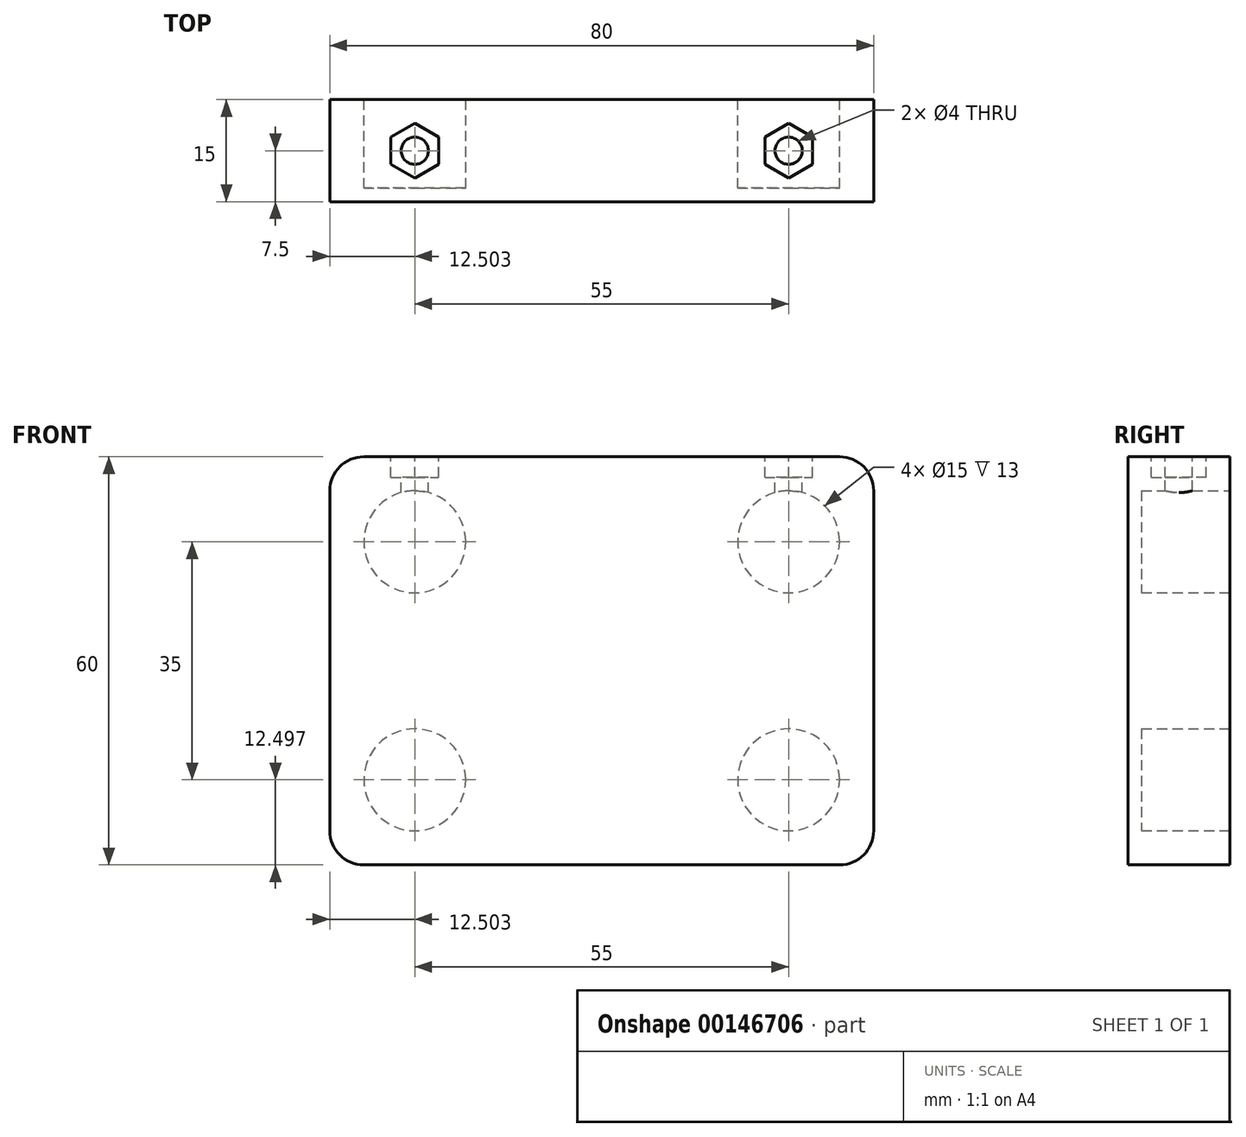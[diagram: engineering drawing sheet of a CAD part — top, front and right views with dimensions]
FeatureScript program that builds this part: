
annotation { "Feature Type Name" : "Feature", "Feature Type Description" : "" }
export const myFeature = defineFeature(function(context is Context, id is Id, definition is map)
    precondition{}
    {
        {
            var Q0;
            Q0=qCreatedBy(makeId("Front.planeOp"),FACE);
            var sketch = newSketch(context, id + "F0", { "sketchPlane" : qUnion([Q0])});
            skLineSegment(sketch, "E0.bottom", {"start": v(-70.09, 32.8) * mm, "end": v(-0.09, 32.8) * mm});
            skLineSegment(sketch, "E0.top", {"start": v(-70.09, -27.2) * mm, "end": v(-0.09, -27.2) * mm});
            skLineSegment(sketch, "E0.left", {"start": v(-75.09, 27.8) * mm, "end": v(-75.09, -22.2) * mm});
            skLineSegment(sketch, "E0.right", {"start": v(4.91, 27.8) * mm, "end": v(4.91, -22.2) * mm});
            skArc(sketch, "E1", {"start": v(-70.09, 32.8) * mm, "mid": v(-73.62, 31.34) * mm, "end": v(-75.09, 27.8) * mm});
            skArc(sketch, "E2", {"start": v(4.91, 27.8) * mm, "mid": v(3.45, 31.34) * mm, "end": v(-0.09, 32.8) * mm});
            skArc(sketch, "E3", {"start": v(-0.09, -27.2) * mm, "mid": v(3.45, -25.73) * mm, "end": v(4.91, -22.2) * mm});
            skArc(sketch, "E4", {"start": v(-75.09, -22.2) * mm, "mid": v(-73.62, -25.73) * mm, "end": v(-70.09, -27.2) * mm});
            skSolve(sketch);
        }
        {
            var Q0;
            Q0 = qSketchRegion(id + "F0", true);
            extrude(context, id + "F1", {"entities" : qUnion([Q0]), "depth" : 15 * mm});
        }
        {
            var Q0;
            Q0=makeQuery(id+"F1.opExtrude","CAP_FACE",FACE,{"disambiguationData":[OSD([sQuery(id+"F0.wireOp",EDGE,"E0.bottom"),sQuery(id+"F0.wireOp",EDGE,"E0.top"),sQuery(id+"F0.wireOp",EDGE,"E0.left"),sQuery(id+"F0.wireOp",EDGE,"E0.right"),sQuery(id+"F0.wireOp",EDGE,"E1"),sQuery(id+"F0.wireOp",EDGE,"E2"),sQuery(id+"F0.wireOp",EDGE,"E3"),sQuery(id+"F0.wireOp",EDGE,"E4")])],"isStart":true});
            var sketch = newSketch(context, id + "F2", { "sketchPlane" : qUnion([Q0])});
            skCircle(sketch, "E5", {"center": v(7.59, 20.3) * mm, "radius": 7.5 * mm});
            skCircle(sketch, "E6", {"center": v(62.59, 20.3) * mm, "radius": 7.5 * mm});
            skCircle(sketch, "E7", {"center": v(62.59, -14.7) * mm, "radius": 7.5 * mm});
            skCircle(sketch, "E8", {"center": v(7.59, -14.7) * mm, "radius": 7.5 * mm});
            skSolve(sketch);
        }
        {
            var Q0;
            Q0 = qSketchRegion(id + "F2", true);
            extrude(context, id + "F3", {"entities" : qUnion([Q0]), "operationType" : NewBodyOperationType.REMOVE, "oppositeDirection" : true, "depth" : 13 * mm});
        }
        {
            var Q0;
            Q0=makeQuery(id+"F1.opExtrude","SWEPT_FACE",FACE,{"disambiguationData":[OSD([sQuery(id+"F0.wireOp",EDGE,"E0.bottom")])]});
            var sketch = newSketch(context, id + "F4", { "sketchPlane" : qUnion([Q0])});
            skCircle(sketch, "E9", {"center": v(-62.59, -7.5) * mm, "radius": 2 * mm});
            skCircle(sketch, "E10", {"center": v(-7.59, -7.5) * mm, "radius": 2 * mm});
            skSolve(sketch);
        }
        {
            var Q0;
            Q0 = qSketchRegion(id + "F4", true);
            extrude(context, id + "F5", {"entities" : qUnion([Q0]), "operationType" : NewBodyOperationType.REMOVE, "oppositeDirection" : true, "depth" : 6 * mm});
        }
        {
            var Q0;
            Q0=makeQuery(id+"F1.opExtrude","SWEPT_FACE",FACE,{"disambiguationData":[OSD([sQuery(id+"F0.wireOp",EDGE,"E0.bottom")])]});
            var sketch = newSketch(context, id + "F6", { "sketchPlane" : qUnion([Q0])});
            skCircle(sketch, "E11.cCircle", {"center": v(-62.59, -7.5) * mm, "radius": 3.5 * mm, "construction": true});
            skLineSegment(sketch, "E11.0", {"start": v(-59.09, -5.48) * mm, "end": v(-59.09, -9.52) * mm});
            skLineSegment(sketch, "E11.1", {"start": v(-59.09, -9.52) * mm, "end": v(-62.59, -11.54) * mm});
            skLineSegment(sketch, "E11.2", {"start": v(-62.59, -11.54) * mm, "end": v(-66.09, -9.52) * mm});
            skLineSegment(sketch, "E11.3", {"start": v(-66.09, -9.52) * mm, "end": v(-66.09, -5.48) * mm});
            skLineSegment(sketch, "E11.4", {"start": v(-66.09, -5.48) * mm, "end": v(-62.59, -3.46) * mm});
            skLineSegment(sketch, "E11.5", {"start": v(-62.59, -3.46) * mm, "end": v(-59.09, -5.48) * mm});
            skPoint(sketch, "E11.0.midPoint", {"position": v(-59.09, -7.5) * mm});
            skCircle(sketch, "E12.cCircle", {"center": v(-7.59, -7.5) * mm, "radius": 3.5 * mm, "construction": true});
            skLineSegment(sketch, "E12.0", {"start": v(-4.09, -5.48) * mm, "end": v(-4.09, -9.52) * mm});
            skLineSegment(sketch, "E12.1", {"start": v(-4.09, -9.52) * mm, "end": v(-7.59, -11.54) * mm});
            skLineSegment(sketch, "E12.2", {"start": v(-7.59, -11.54) * mm, "end": v(-11.09, -9.52) * mm});
            skLineSegment(sketch, "E12.3", {"start": v(-11.09, -9.52) * mm, "end": v(-11.09, -5.48) * mm});
            skLineSegment(sketch, "E12.4", {"start": v(-11.09, -5.48) * mm, "end": v(-7.59, -3.46) * mm});
            skLineSegment(sketch, "E12.5", {"start": v(-7.59, -3.46) * mm, "end": v(-4.09, -5.48) * mm});
            skPoint(sketch, "E12.0.midPoint", {"position": v(-4.09, -7.5) * mm});
            skSolve(sketch);
        }
        {
            var Q0;
            Q0 = qSketchRegion(id + "F6", true);
            extrude(context, id + "F7", {"entities" : qUnion([Q0]), "operationType" : NewBodyOperationType.REMOVE, "oppositeDirection" : true, "depth" : 3 * mm});
        }
    });
